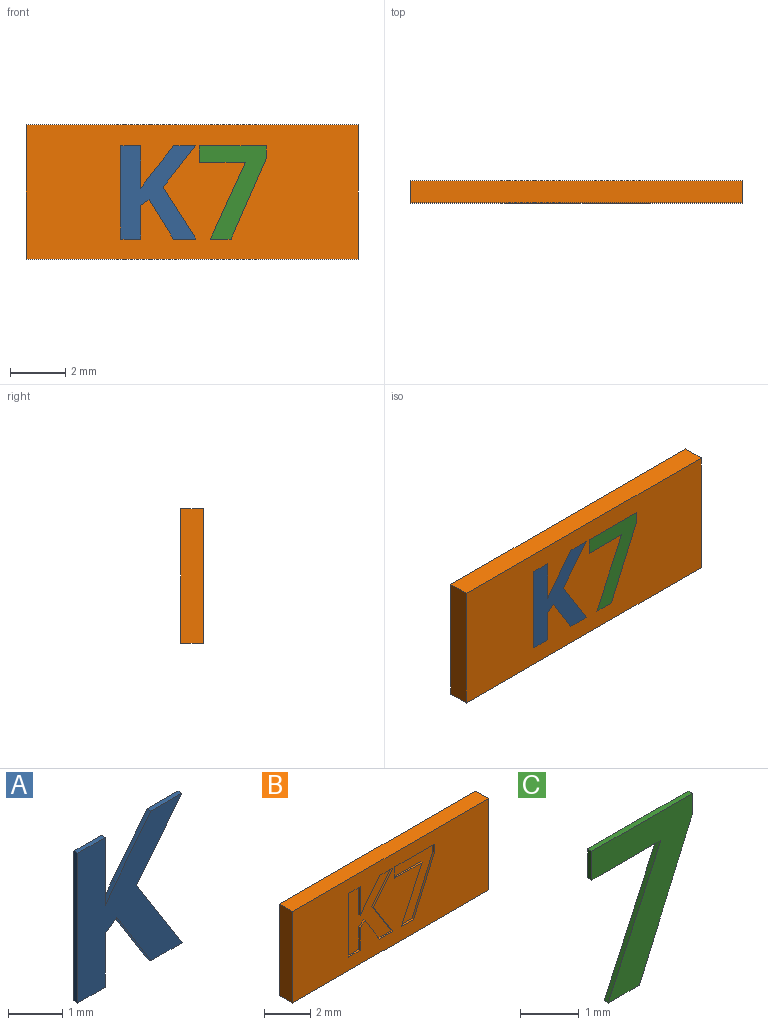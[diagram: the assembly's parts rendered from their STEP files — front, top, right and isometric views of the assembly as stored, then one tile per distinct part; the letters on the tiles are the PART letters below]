
ASSEMBLY  parts=3 mates=2
PART A: 15 faces, bbox 2.7x0.1x3.4 mm
  f0: plane 3.37x2.71mm, normal (0,-1,0), area 5.2mm2, adj f1,f2,f3,f4,f5,f6,f7,f8
  f1: plane 1.49x1.18mm, normal (0.79,0,-0.62), area 0.2mm2, adj f0,f2,f11,f13
  f2: plane 0.79x0.1mm, normal (0,0,1), area 0.1mm2, adj f0,f1,f3,f11
  f3: plane 1.15x0.91mm, normal (-0.78,0,0.62), area 0.1mm2, adj f0,f2,f4,f11
  f4: plane 0.4x0.28mm, normal (-0.82,0,0.58), area 0mm2, adj f0,f3,f5,f11
  f5: plane 1.54x0.1mm, normal (1,0,0), area 0.2mm2, adj f0,f4,f6,f11
  f6: plane 0.72x0.1mm, normal (0,0,1), area 0.1mm2, adj f0,f5,f7,f11
  f7: plane 3.37x0.1mm, normal (-1,0,0), area 0.3mm2, adj f0,f6,f8,f11
  f8: plane 0.72x0.1mm, normal (0,0,-1), area 0.1mm2, adj f0,f7,f9,f11
  f9: plane 1.2x0.1mm, normal (1,0,0), area 0.1mm2, adj f0,f8,f10,f11
  f10: plane 0.3x0.22mm, normal (0.58,0,-0.81), area 0mm2, adj f0,f9,f11,f12
  f11: plane 3.37x2.71mm, normal (0,1,0), area 5.2mm2, adj f1,f2,f3,f4,f5,f6,f7,f8
  f12: plane 1.42x0.88mm, normal (-0.85,0,-0.53), area 0.2mm2, adj f0,f10,f11,f14
  f13: plane 1.88x1.19mm, normal (0.85,0,0.53), area 0.2mm2, adj f0,f1,f11,f14
  f14: plane 0.81x0.1mm, normal (0,0,-1), area 0.1mm2, adj f0,f11,f12,f13
PART B: 28 faces, bbox 12x0.8x4.9 mm
  f0: plane 12x4.85mm, normal (0,-1,0), area 49.6mm2, adj f1,f2,f3,f4,f6,f7,f8,f9
  f1: plane 12x0.8mm, normal (0,0,-1), area 9.6mm2, adj f0,f2,f4,f5
  f2: plane 4.85x0.8mm, normal (1,0,0), area 3.9mm2, adj f0,f1,f3,f5
  f3: plane 12x0.8mm, normal (0,0,1), area 9.6mm2, adj f0,f2,f4,f5
  f4: plane 4.85x0.8mm, normal (-1,0,0), area 3.9mm2, adj f0,f1,f3,f5
  f5: plane 12x4.85mm, normal (0,1,0), area 58.2mm2, adj f1,f2,f3,f4
  f6: plane 0.75x0.1mm, normal (0,0,1), area 0.1mm2, adj f0,f7,f12,f13
  f7: plane 2.92x1.28mm, normal (-0.92,0,0.4), area 0.3mm2, adj f0,f6,f8,f13
  f8: plane 0.45x0.1mm, normal (-1,0,0), area 0mm2, adj f0,f7,f9,f13
  f9: plane 2.42x0.1mm, normal (0,0,-1), area 0.2mm2, adj f0,f8,f10,f13
  f10: plane 0.6x0.1mm, normal (1,0,0), area 0.1mm2, adj f0,f9,f11,f13
  f11: plane 1.66x0.1mm, normal (0,0,1), area 0.2mm2, adj f0,f10,f12,f13
  f12: plane 2.77x1.27mm, normal (0.91,0,-0.42), area 0.3mm2, adj f0,f6,f11,f13
  f13: plane 3.37x2.42mm, normal (0,-1,0), area 3.4mm2, adj f6,f7,f8,f9,f10,f11,f12
  f14: plane 1.88x1.19mm, normal (-0.85,0,-0.53), area 0.2mm2, adj f0,f15,f26,f27
  f15: plane 1.49x1.18mm, normal (-0.79,0,0.62), area 0.2mm2, adj f0,f14,f16,f27
  f16: plane 0.79x0.1mm, normal (0,0,-1), area 0.1mm2, adj f0,f15,f17,f27
  f17: plane 1.15x0.91mm, normal (0.78,0,-0.62), area 0.1mm2, adj f0,f16,f18,f27
  f18: plane 0.4x0.28mm, normal (0.82,0,-0.58), area 0mm2, adj f0,f17,f19,f27
  f19: plane 1.54x0.1mm, normal (-1,0,0), area 0.2mm2, adj f0,f18,f20,f27
  f20: plane 0.72x0.1mm, normal (0,0,-1), area 0.1mm2, adj f0,f19,f21,f27
  f21: plane 3.37x0.1mm, normal (1,0,0), area 0.3mm2, adj f0,f20,f22,f27
  f22: plane 0.72x0.1mm, normal (0,0,1), area 0.1mm2, adj f0,f21,f23,f27
  f23: plane 1.2x0.1mm, normal (-1,0,0), area 0.1mm2, adj f0,f22,f24,f27
  f24: plane 0.3x0.22mm, normal (-0.58,0,0.81), area 0mm2, adj f0,f23,f25,f27
  f25: plane 1.42x0.88mm, normal (0.85,0,0.53), area 0.2mm2, adj f0,f24,f26,f27
  f26: plane 0.81x0.1mm, normal (0,0,1), area 0.1mm2, adj f0,f14,f25,f27
  f27: plane 3.37x2.71mm, normal (0,-1,0), area 5.2mm2, adj f14,f15,f16,f17,f18,f19,f20,f21
PART C: 9 faces, bbox 2.4x0.1x3.4 mm
  f0: plane 3.37x2.42mm, normal (0,-1,0), area 3.4mm2, adj f1,f2,f3,f4,f6,f7,f8
  f1: plane 2.92x1.28mm, normal (0.92,0,-0.4), area 0.3mm2, adj f0,f2,f5,f7
  f2: plane 0.45x0.1mm, normal (1,0,0), area 0mm2, adj f0,f1,f3,f5
  f3: plane 2.42x0.1mm, normal (0,0,1), area 0.2mm2, adj f0,f2,f4,f5
  f4: plane 0.6x0.1mm, normal (-1,0,0), area 0.1mm2, adj f0,f3,f5,f6
  f5: plane 3.37x2.42mm, normal (0,1,0), area 3.4mm2, adj f1,f2,f3,f4,f6,f7,f8
  f6: plane 1.66x0.1mm, normal (0,0,-1), area 0.2mm2, adj f0,f4,f5,f8
  f7: plane 0.75x0.1mm, normal (0,0,-1), area 0.1mm2, adj f0,f1,f5,f8
  f8: plane 2.77x1.27mm, normal (-0.91,0,0.42), area 0.3mm2, adj f0,f5,f6,f7
PLACE A t=(-0.27,0.4,-0.03)mm
PLACE B t=(0.03,0.4,-0.03)mm
PLACE C t=(0.03,0.4,-0.03)mm
MATE fastened C.f0 <-> B.f0  axis (0,-1,0) through (0.69,-0.4,-1.73)mm
MATE fastened A.f0 <-> B.f0  axis (0,-1,0) through (-2.54,-0.4,-1.73)mm
